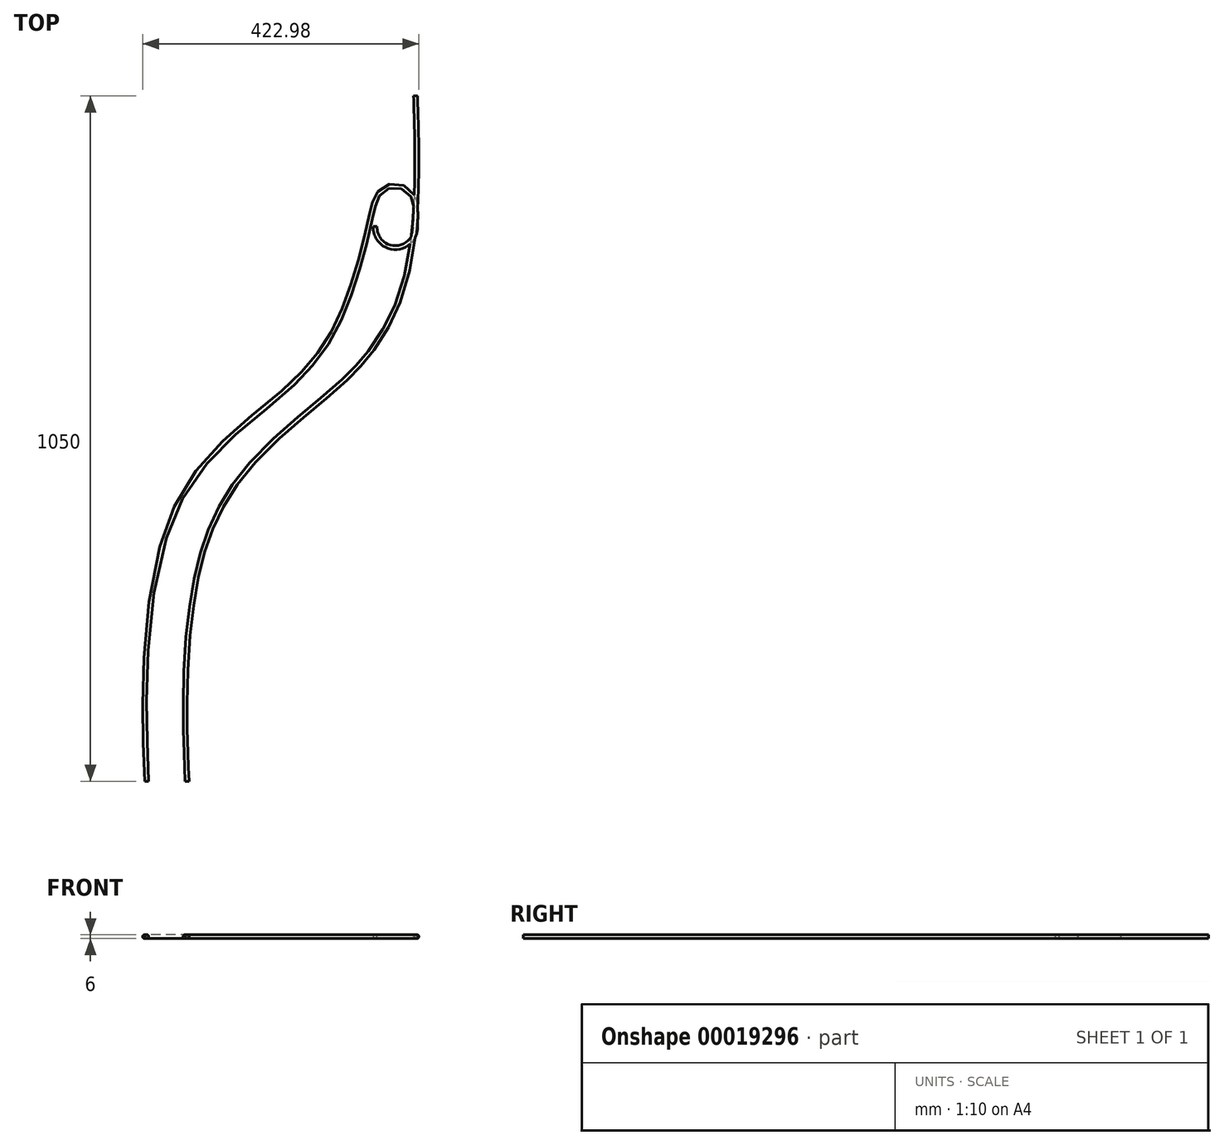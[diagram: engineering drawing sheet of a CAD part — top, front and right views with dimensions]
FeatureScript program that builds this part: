
annotation { "Feature Type Name" : "Feature", "Feature Type Description" : "" }
export const myFeature = defineFeature(function(context is Context, id is Id, definition is map)
    precondition{}
    {
        {
            var Q0;
            Q0=qCreatedBy(makeId("Top.planeOp"),FACE);
            var sketch = newSketch(context, id + "F0", { "sketchPlane" : qUnion([Q0])});
            skFitSpline(sketch, "E0", {"points": [v(350, 850) * mm, v(350, 879.54) * mm, v(277.88, 666.1) * mm, v(37.41, 396.01) * mm, v(0, 0) * mm], "startDerivative": vector(0, -249.42) * mm, "endDerivative": vector(0, -244.5) * mm, "construction": true});
            skLineSegment(sketch, "E1", {"start": v(0, 0) * mm, "end": v(0, 67.22) * mm, "construction": true});
            skLineSegment(sketch, "E2", {"start": v(350, 879.54) * mm, "end": v(350, 850) * mm, "construction": true});
            skFitSpline(sketch, "E3.0", {"points": [v(319, 850) * mm, v(319, 849.9) * mm, v(319, 849.68) * mm, v(319, 849.36) * mm, v(319, 849.1) * mm, v(319, 848.87) * mm, v(319, 848.7) * mm, v(319.01, 848.52) * mm, v(319.02, 848.32) * mm, v(319.02, 848.1) * mm, v(319.03, 847.87) * mm, v(319.04, 847.58) * mm, v(319.06, 847.3) * mm, v(319.07, 847.03) * mm, v(319.08, 846.8) * mm, v(319.1, 846.54) * mm, v(319.13, 846.23) * mm, v(319.16, 845.86) * mm, v(319.2, 845.4) * mm, v(319.27, 844.84) * mm, v(319.36, 844.23) * mm, v(319.46, 843.61) * mm, v(319.55, 843.07) * mm, v(319.68, 842.42) * mm, v(319.85, 841.64) * mm, v(320.1, 840.67) * mm, v(320.45, 839.45) * mm, v(320.9, 838.13) * mm, v(321.41, 836.82) * mm, v(321.92, 835.67) * mm, v(322.57, 834.33) * mm, v(323.45, 832.76) * mm, v(324.65, 830.9) * mm, v(326.3, 828.72) * mm, v(328.63, 826.22) * mm, v(331.35, 823.92) * mm, v(334.15, 822.09) * mm, v(336.58, 820.78) * mm, v(339.34, 819.6) * mm, v(342.4, 818.65) * mm, v(345.72, 818) * mm, v(349.17, 817.7) * mm, v(352.64, 817.8) * mm, v(355.99, 818.27) * mm, v(359.12, 819.06) * mm, v(361.96, 820.1) * mm, v(364.47, 821.28) * mm, v(366.65, 822.55) * mm, v(368.52, 823.84) * mm, v(370.65, 825.54) * mm, v(372.7, 827.54) * mm, v(374.48, 829.64) * mm, v(375.78, 831.45) * mm, v(376.74, 832.98) * mm, v(377.47, 834.3) * mm, v(378.03, 835.42) * mm, v(378.62, 836.72) * mm, v(379.13, 838.01) * mm, v(379.54, 839.22) * mm, v(379.83, 840.18) * mm, v(380.04, 840.96) * mm, v(380.2, 841.6) * mm, v(380.37, 842.32) * mm, v(380.5, 843.02) * mm, v(380.62, 843.66) * mm, v(380.7, 844.16) * mm, v(380.76, 844.57) * mm, v(380.8, 844.9) * mm, v(380.84, 845.2) * mm, v(380.86, 845.44) * mm, v(380.9, 845.72) * mm, v(380.92, 846.01) * mm, v(380.95, 846.3) * mm, v(380.97, 846.55) * mm, v(380.99, 846.76) * mm, v(381, 846.96) * mm, v(381.01, 847.13) * mm, v(381.02, 847.3) * mm, v(381.04, 847.5) * mm, v(381.05, 847.76) * mm, v(381.06, 848.04) * mm, v(381.08, 848.32) * mm, v(381.1, 848.6) * mm, v(381.1, 848.9) * mm, v(381.12, 849.2) * mm, v(381.13, 849.5) * mm, v(381.14, 849.91) * mm, v(381.16, 850.46) * mm, v(381.19, 851.15) * mm, v(381.2, 851.9) * mm, v(381.23, 852.67) * mm, v(381.25, 853.5) * mm, v(381.28, 854.35) * mm, v(381.3, 855.53) * mm, v(381.34, 857.1) * mm, v(381.37, 859.08) * mm, v(381.4, 861.14) * mm, v(381.42, 863.26) * mm, v(381.43, 865.42) * mm, v(381.43, 867.6) * mm, v(381.42, 869.76) * mm, v(381.4, 871.9) * mm, v(381.36, 874) * mm, v(381.3, 876.08) * mm, v(381.2, 878.11) * mm, v(381.1, 879.82) * mm, v(381, 881.24) * mm, v(380.9, 882.17) * mm, v(380.81, 882.96) * mm, v(380.71, 883.8) * mm, v(380.55, 884.93) * mm, v(380.28, 886.5) * mm, v(379.93, 888.05) * mm, v(379.53, 889.56) * mm, v(379.13, 890.85) * mm, v(378.6, 892.36) * mm, v(377.86, 894.13) * mm, v(376.83, 896.24) * mm, v(375.32, 898.77) * mm, v(373.47, 901.26) * mm, v(371.45, 903.46) * mm, v(369.6, 905.19) * mm, v(367.37, 906.94) * mm, v(364.73, 908.63) * mm, v(361.66, 910.18) * mm, v(358.2, 911.44) * mm, v(354.46, 912.32) * mm, v(350.6, 912.72) * mm, v(346.78, 912.65) * mm, v(343.18, 912.15) * mm, v(339.9, 911.3) * mm, v(337.01, 910.23) * mm, v(334.52, 909.03) * mm, v(332.39, 907.77) * mm, v(330.59, 906.52) * mm, v(328.56, 904.91) * mm, v(326.61, 903.06) * mm, v(324.92, 901.14) * mm, v(323.66, 899.49) * mm, v(322.7, 898.07) * mm, v(321.7, 896.44) * mm, v(320.82, 894.78) * mm, v(320.07, 893.17) * mm, v(319.5, 891.81) * mm, v(319.05, 890.62) * mm, v(318.66, 889.54) * mm, v(318.31, 888.52) * mm, v(318, 887.55) * mm, v(317.61, 886.27) * mm, v(317.16, 884.7) * mm, v(316.65, 882.79) * mm, v(316.13, 880.8) * mm, v(315.6, 878.7) * mm, v(315.07, 876.5) * mm, v(314.52, 874.18) * mm, v(313.95, 871.74) * mm, v(313.16, 868.32) * mm, v(312.11, 863.73) * mm, v(310.75, 857.74) * mm, v(309.27, 851.29) * mm, v(307.68, 844.4) * mm, v(305.96, 837.12) * mm, v(304.11, 829.48) * mm, v(301.48, 818.85) * mm, v(297.86, 804.84) * mm, v(292.95, 787.18) * mm, v(287.47, 768.99) * mm, v(281.4, 750.59) * mm, v(274.74, 732.31) * mm, v(268.7, 717.47) * mm, v(263.57, 706) * mm, v(259.58, 697.64) * mm, v(256.15, 690.92) * mm, v(253.34, 685.7) * mm, v(251.2, 681.89) * mm, v(249.04, 678.16) * mm, v(246.09, 673.26) * mm, v(242.29, 667.3) * mm, v(237.56, 660.38) * mm, v(231.04, 651.44) * mm, v(222.49, 640.75) * mm, v(211.63, 628.55) * mm, v(200.22, 616.86) * mm, v(184.33, 601.8) * mm, v(163.34, 583.63) * mm, v(136.9, 561.98) * mm, v(109.89, 539.47) * mm, v(87.5, 519.1) * mm, v(70.1, 501.29) * mm, v(57.44, 487.03) * mm, v(45.29, 471.75) * mm, v(33.8, 455.32) * mm, v(24.87, 440.6) * mm, v(18.2, 428.17) * mm, v(14.24, 420.11) * mm, v(11.2, 413.5) * mm, v(9, 408.44) * mm, v(6.85, 403.3) * mm, v(4.1, 396.37) * mm, v(0.86, 387.55) * mm, v(-3.96, 373.13) * mm, v(-9.32, 354.59) * mm, v(-14.8, 331.64) * mm, v(-19.41, 308.16) * mm, v(-23.25, 284.32) * mm, v(-26.38, 260.27) * mm, v(-29.7, 228.16) * mm, v(-32.42, 188.4) * mm, v(-33.9, 142.7) * mm, v(-34.04, 107.5) * mm, v(-33.72, 81.84) * mm, v(-33.33, 64.04) * mm, v(-32.84, 47.85) * mm, v(-32.3, 33.5) * mm, v(-31.88, 23.23) * mm, v(-31.58, 16.15) * mm, v(-31.38, 11.44) * mm, v(-31.2, 7.37) * mm, v(-31.09, 4) * mm, v(-31.02, 1.84) * mm, v(-31, 0.59) * mm, v(-31, 0.15) * mm, v(-31, 0) * mm]});
            skFitSpline(sketch, "E4.0", {"points": [v(381, 1050) * mm, v(381, 1049.78) * mm, v(381, 1049.26) * mm, v(381.02, 1047.9) * mm, v(381.06, 1045.69) * mm, v(381.14, 1042.36) * mm, v(381.3, 1037.12) * mm, v(381.53, 1029.18) * mm, v(381.87, 1017.74) * mm, v(382.21, 1004.63) * mm, v(382.52, 990.1) * mm, v(382.76, 974.4) * mm, v(382.89, 957.74) * mm, v(382.86, 940.36) * mm, v(382.64, 922.5) * mm, v(382.19, 904.35) * mm, v(381.58, 889.18) * mm, v(380.93, 877.13) * mm, v(380.16, 865.16) * mm, v(378.98, 850.36) * mm, v(377.12, 832.84) * mm, v(373.99, 809.8) * mm, v(368.69, 781.6) * mm, v(359.61, 748.7) * mm, v(349.36, 722.13) * mm, v(339.33, 701.47) * mm, v(330.83, 686.3) * mm, v(322.9, 673.97) * mm, v(316.04, 664.28) * mm, v(310.63, 657.11) * mm, v(305.9, 651.22) * mm, v(301.98, 646.56) * mm, v(297.96, 641.94) * mm, v(292.82, 636.27) * mm, v(284.35, 627.4) * mm, v(273.34, 616.62) * mm, v(259.58, 604.04) * mm, v(245.4, 591.7) * mm, v(230.94, 579.44) * mm, v(216.29, 567.18) * mm, v(196.66, 550.68) * mm, v(172.23, 529.5) * mm, v(143.99, 502.46) * mm, v(122.05, 478) * mm, v(105.85, 456.9) * mm, v(94.45, 440.24) * mm, v(85.67, 425.54) * mm, v(79.1, 413.25) * mm, v(74.43, 403.75) * mm, v(70.75, 395.58) * mm, v(67.94, 388.88) * mm, v(65.9, 383.78) * mm, v(63.92, 378.58) * mm, v(61.36, 371.51) * mm, v(58.32, 362.43) * mm, v(54.91, 351.18) * mm, v(50.69, 335.76) * mm, v(46, 315.78) * mm, v(41.26, 290.97) * mm, v(37.37, 265.6) * mm, v(34.26, 239.95) * mm, v(31.06, 205.75) * mm, v(29.15, 172.08) * mm, v(28.23, 139.98) * mm, v(27.94, 116.96) * mm, v(28, 95.24) * mm, v(28.3, 75.1) * mm, v(28.78, 56.75) * mm, v(29.35, 40.48) * mm, v(29.85, 28.83) * mm, v(30.21, 20.77) * mm, v(30.46, 15.37) * mm, v(30.67, 10.64) * mm, v(30.82, 7.23) * mm, v(30.9, 4.81) * mm, v(30.95, 3.13) * mm, v(30.99, 1.55) * mm, v(31, 0.53) * mm, v(31, 0) * mm]});
            skLineSegment(sketch, "E5", {"start": v(-31, 0) * mm, "end": v(31, 0) * mm, "construction": true});
            skLineSegment(sketch, "E6", {"start": v(308.97, 850) * mm, "end": v(381, 850) * mm, "construction": true});
            skLineSegment(sketch, "E7", {"start": v(-73.04, 0) * mm, "end": v(75.16, 0) * mm, "construction": true});
            skSolve(sketch);
        }
        {
            var Q0;
            Q0=qCreatedBy(makeId("Front.planeOp"),FACE);
            var sketch = newSketch(context, id + "F1", { "sketchPlane" : qUnion([Q0])});
            skCircle(sketch, "E8", {"center": v(-31, 0) * mm, "radius": 3 * mm});
            skSolve(sketch);
        }
        {
            var Q0;
            Q0=makeQuery(id+"F1.imprint","IMPRINT",FACE,{"disambiguationData":[TD([[makeQuery(id+"F1.imprint","IMPRINT",EDGE,{"derivedFrom":sQuery(id+"F1.wireOp",EDGE,"E8")}),1.0]])]});
            var Q1;
            Q1=sQuery(id+"F0.wireOp",EDGE,"E3.0");
            sweep(context, id + "F2", {"profiles" : qUnion([Q0]), "path" : qUnion([Q1])});
        }
        {
            var Q0;
            Q0=qCreatedBy(makeId("Front.planeOp"),FACE);
            var sketch = newSketch(context, id + "F3", { "sketchPlane" : qUnion([Q0])});
            skCircle(sketch, "E9", {"center": v(31, 0) * mm, "radius": 3 * mm});
            skSolve(sketch);
        }
        {
            var Q0;
            Q0=makeQuery(id+"F3.imprint","IMPRINT",FACE,{"disambiguationData":[TD([[makeQuery(id+"F3.imprint","IMPRINT",EDGE,{"derivedFrom":sQuery(id+"F3.wireOp",EDGE,"E9")}),1.0]])]});
            var Q1;
            Q1=sQuery(id+"F0.wireOp",EDGE,"E4.0");
            sweep(context, id + "F4", {"profiles" : qUnion([Q0]), "path" : qUnion([Q1])});
        }
    });
